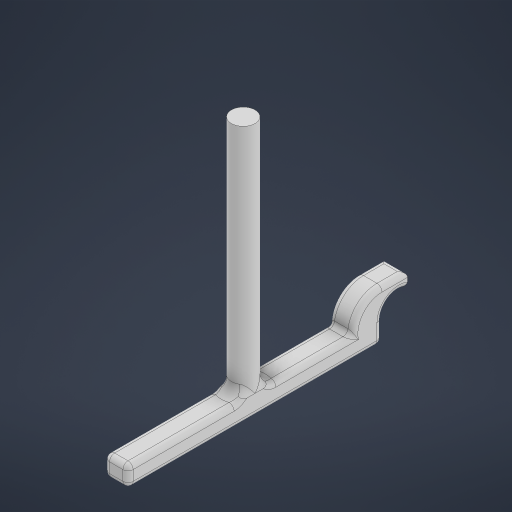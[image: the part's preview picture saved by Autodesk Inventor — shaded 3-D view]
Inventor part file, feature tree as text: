
AUTODESK INVENTOR PART (.ipt)
format: ipt  version: 2024.1 (Build 281209000, 209)  size: 565,760 bytes
history: native  units: mm
features: extrude x3, fillet x3, sketch x3
ambient origin geometry x8: Origin, YZ Plane, XZ Plane, XY Plane, X Axis, Y Axis, Z Axis, Center Point
bodies: Solid1 (feature_tree)
feature tree (9):
  extrude  "Extrusion1"  Depth=50.0mm TaperAngle=0.0deg
  extrude  "Extrusion2"  Depth=4.0mm TaperAngle=0.0deg
  extrude  "Extrusion3"  Depth=2.0mm
  fillet  "Fillet3"  Radius=1.0mm
  fillet  "Fillet4"  Radius=1.0mm
  fillet  "Fillet5"  [1 undecoded]
  sketch  "Sketch1"  dims[d0=4.64mm d1=50.0mm d2=0.0mm]
  sketch  "Sketch2"  dims[d4=50.0mm d5=4.0mm d6=0.0mm]
  sketch  "Sketch3"  dims[d7=10.0mm d8=0.0mm d11=2.0mm d12=1.0mm d13=1.0mm d10=0.0mm]
note: 1 required parameter value undecoded (feature->parameter linkage not recoverable at this tier; creation-order binding heuristic only, values carry confidence <= 0.55)
